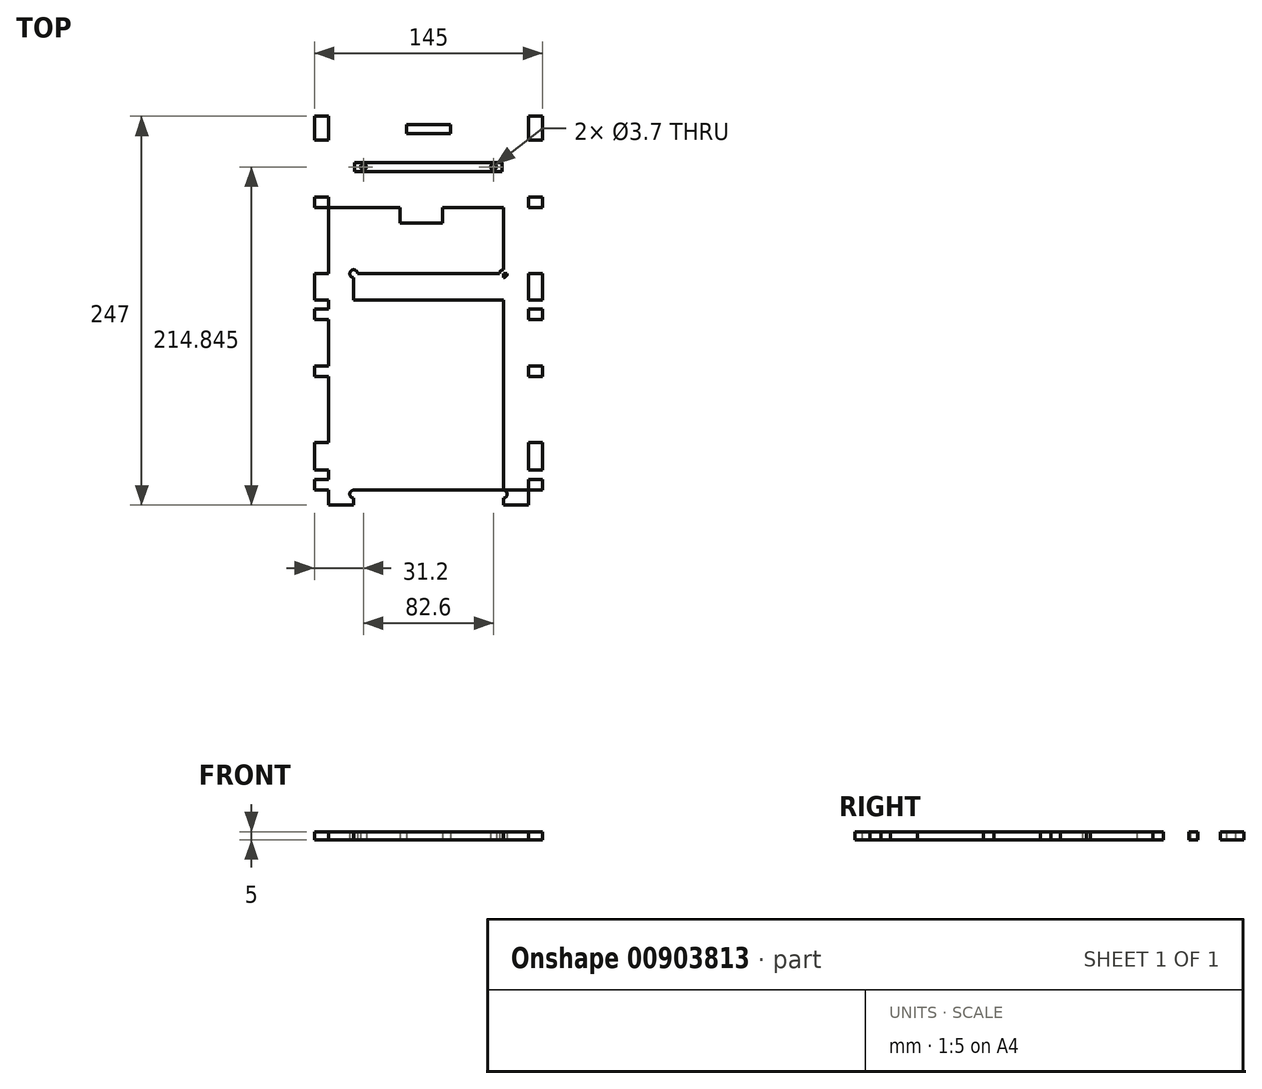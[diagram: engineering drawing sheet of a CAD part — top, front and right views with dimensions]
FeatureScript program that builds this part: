
annotation { "Feature Type Name" : "Feature", "Feature Type Description" : "" }
export const myFeature = defineFeature(function(context is Context, id is Id, definition is map)
    precondition{}
    {
        {
            var Q0;
            Q0=qCreatedBy(makeId("Top.planeOp"),FACE);
            var sketch = newSketch(context, id + "F0", { "sketchPlane" : qUnion([Q0])});
            skLineSegment(sketch, "E0.bottom", {"start": v(-77.4, -23.3) * mm, "end": v(49.6, -23.3) * mm});
            skLineSegment(sketch, "E0.top", {"start": v(-77.4, 223.7) * mm, "end": v(49.6, 223.7) * mm});
            skLineSegment(sketch, "E0.left", {"start": v(-77.4, -23.3) * mm, "end": v(-77.4, 223.7) * mm});
            skLineSegment(sketch, "E0.right", {"start": v(49.6, -23.3) * mm, "end": v(49.6, 223.7) * mm});
            skLineSegment(sketch, "E1", {"start": v(49.6, 223.7) * mm, "end": v(58.6, 223.7) * mm});
            skLineSegment(sketch, "E2", {"start": v(-86.4, 223.7) * mm, "end": v(-77.4, 223.7) * mm});
            skLineSegment(sketch, "E3", {"start": v(58.6, 223.7) * mm, "end": v(58.6, 208.7) * mm});
            skLineSegment(sketch, "E4", {"start": v(58.6, 208.7) * mm, "end": v(49.6, 208.7) * mm});
            skLineSegment(sketch, "E5", {"start": v(49.6, 208.7) * mm, "end": v(49.6, 172.5) * mm});
            skLineSegment(sketch, "E6", {"start": v(58.6, 172.5) * mm, "end": v(49.6, 172.5) * mm});
            skLineSegment(sketch, "E7", {"start": v(58.6, 172.5) * mm, "end": v(58.6, 165.8) * mm});
            skLineSegment(sketch, "E8", {"start": v(58.6, 165.8) * mm, "end": v(49.6, 165.8) * mm});
            skLineSegment(sketch, "E9", {"start": v(49.6, 165.8) * mm, "end": v(49.6, 123.8) * mm});
            skLineSegment(sketch, "E10", {"start": v(49.6, 123.8) * mm, "end": v(58.6, 123.8) * mm});
            skLineSegment(sketch, "E11", {"start": v(58.6, 107.1) * mm, "end": v(58.6, 123.8) * mm});
            skLineSegment(sketch, "E12", {"start": v(58.6, 107.1) * mm, "end": v(49.6, 107.1) * mm});
            skLineSegment(sketch, "E13", {"start": v(49.6, 107.1) * mm, "end": v(49.6, 101.2) * mm});
            skLineSegment(sketch, "E14", {"start": v(49.6, 101.2) * mm, "end": v(58.6, 101.2) * mm});
            skLineSegment(sketch, "E15", {"start": v(58.6, 101.2) * mm, "end": v(58.6, 94.5) * mm});
            skLineSegment(sketch, "E16", {"start": v(58.6, 94.5) * mm, "end": v(49.6, 94.5) * mm});
            skLineSegment(sketch, "E17", {"start": v(49.6, 94.5) * mm, "end": v(49.6, 65.1) * mm});
            skLineSegment(sketch, "E18", {"start": v(49.6, 65.1) * mm, "end": v(58.6, 65.1) * mm});
            skLineSegment(sketch, "E19", {"start": v(58.6, 65.1) * mm, "end": v(58.6, 58.3) * mm});
            skLineSegment(sketch, "E20", {"start": v(49.6, 58.3) * mm, "end": v(58.6, 58.3) * mm});
            skLineSegment(sketch, "E21", {"start": v(49.6, 58.3) * mm, "end": v(49.6, 16.4) * mm});
            skLineSegment(sketch, "E22", {"start": v(49.6, 16.4) * mm, "end": v(58.6, 16.4) * mm});
            skLineSegment(sketch, "E23", {"start": v(58.6, 16.4) * mm, "end": v(58.6, -0.9) * mm});
            skLineSegment(sketch, "E24", {"start": v(58.6, -0.9) * mm, "end": v(49.6, -0.9) * mm});
            skLineSegment(sketch, "E25", {"start": v(49.6, -0.9) * mm, "end": v(49.6, -6.9) * mm});
            skLineSegment(sketch, "E26", {"start": v(49.6, -6.9) * mm, "end": v(58.6, -6.9) * mm});
            skLineSegment(sketch, "E27", {"start": v(49.6, -6.9) * mm, "end": v(49.6, -13.7) * mm});
            skLineSegment(sketch, "E28", {"start": v(49.6, -13.7) * mm, "end": v(58.6, -13.7) * mm});
            skLineSegment(sketch, "E29", {"start": v(58.6, -6.9) * mm, "end": v(58.6, -13.7) * mm});
            skLineSegment(sketch, "E30", {"start": v(49.6, 208.7) * mm, "end": v(-86.4, 208.7) * mm});
            skLineSegment(sketch, "E31", {"start": v(49.6, 172.5) * mm, "end": v(-86.28, 172.5) * mm});
            skLineSegment(sketch, "E32", {"start": v(49.6, 165.8) * mm, "end": v(-86.28, 165.8) * mm});
            skLineSegment(sketch, "E33", {"start": v(49.6, 123.8) * mm, "end": v(-86.4, 123.8) * mm});
            skLineSegment(sketch, "E34", {"start": v(49.6, 107.1) * mm, "end": v(-86.4, 107.1) * mm});
            skLineSegment(sketch, "E35", {"start": v(49.6, 101.2) * mm, "end": v(-86.4, 101.2) * mm});
            skLineSegment(sketch, "E36", {"start": v(49.6, 94.5) * mm, "end": v(-86.4, 94.5) * mm});
            skLineSegment(sketch, "E37", {"start": v(49.6, 65.1) * mm, "end": v(-86.4, 65.1) * mm});
            skLineSegment(sketch, "E38", {"start": v(49.6, 58.3) * mm, "end": v(-86.4, 58.3) * mm});
            skLineSegment(sketch, "E39", {"start": v(49.6, 16.4) * mm, "end": v(-86.4, 16.4) * mm});
            skLineSegment(sketch, "E40", {"start": v(49.6, -0.9) * mm, "end": v(-86.4, -0.9) * mm});
            skLineSegment(sketch, "E41", {"start": v(49.6, -6.9) * mm, "end": v(-86.4, -6.9) * mm});
            skLineSegment(sketch, "E42", {"start": v(49.6, -13.7) * mm, "end": v(-86.4, -13.7) * mm});
            skLineSegment(sketch, "E43", {"start": v(-86.4, -13.7) * mm, "end": v(-86.4, -6.9) * mm});
            skLineSegment(sketch, "E44", {"start": v(-86.4, -0.9) * mm, "end": v(-86.4, 16.4) * mm});
            skLineSegment(sketch, "E45", {"start": v(-86.4, 58.3) * mm, "end": v(-86.4, 65.1) * mm});
            skLineSegment(sketch, "E46", {"start": v(-86.4, 94.5) * mm, "end": v(-86.4, 101.2) * mm});
            skLineSegment(sketch, "E47", {"start": v(-86.4, 107.1) * mm, "end": v(-86.4, 123.8) * mm});
            skLineSegment(sketch, "E48", {"start": v(-86.28, 165.8) * mm, "end": v(-86.28, 172.5) * mm});
            skLineSegment(sketch, "E49", {"start": v(-86.4, 208.7) * mm, "end": v(-86.4, 223.7) * mm});
            skLineSegment(sketch, "E50", {"start": v(49.6, 223.7) * mm, "end": v(49.6, 218.3) * mm});
            skLineSegment(sketch, "E51", {"start": v(49.6, 218.3) * mm, "end": v(-77.4, 218.3) * mm});
            skLineSegment(sketch, "E52", {"start": v(-77.4, 212.6) * mm, "end": v(-77.4, 218.3) * mm});
            skLineSegment(sketch, "E53", {"start": v(-77.4, 212.6) * mm, "end": v(49.6, 212.6) * mm});
            skLineSegment(sketch, "E54", {"start": v(49.6, 212.6) * mm, "end": v(40.9, 212.6) * mm});
            skLineSegment(sketch, "E55", {"start": v(40.9, 212.6) * mm, "end": v(40.9, 218.3) * mm});
            skLineSegment(sketch, "E56", {"start": v(-77.4, 212.6) * mm, "end": v(-68.7, 212.6) * mm});
            skLineSegment(sketch, "E57", {"start": v(-68.7, 218.3) * mm, "end": v(-68.7, 212.6) * mm});
            skLineSegment(sketch, "E58", {"start": v(-68.7, 218.3) * mm, "end": v(-58.5, 218.3) * mm});
            skLineSegment(sketch, "E59", {"start": v(-58.5, 218.3) * mm, "end": v(-58.5, 212.6) * mm});
            skLineSegment(sketch, "E60", {"start": v(40.9, 218.3) * mm, "end": v(30.7, 218.3) * mm});
            skLineSegment(sketch, "E61", {"start": v(30.7, 218.3) * mm, "end": v(30.7, 212.6) * mm});
            skLineSegment(sketch, "E62", {"start": v(30.7, 212.6) * mm, "end": v(10.2, 212.6) * mm});
            skLineSegment(sketch, "E63", {"start": v(10.2, 212.6) * mm, "end": v(10.2, 218.3) * mm});
            skLineSegment(sketch, "E64", {"start": v(10.2, 218.3) * mm, "end": v(30.7, 218.3) * mm});
            skLineSegment(sketch, "E65", {"start": v(-58.5, 212.6) * mm, "end": v(-38, 212.6) * mm});
            skLineSegment(sketch, "E66", {"start": v(-38, 218.3) * mm, "end": v(-58.5, 218.3) * mm});
            skLineSegment(sketch, "E67", {"start": v(-38, 218.3) * mm, "end": v(-38, 212.6) * mm});
            skLineSegment(sketch, "E68", {"start": v(-38, 218.3) * mm, "end": v(-27.8, 218.3) * mm});
            skLineSegment(sketch, "E69", {"start": v(-27.8, 212.6) * mm, "end": v(-27.8, 218.3) * mm});
            skLineSegment(sketch, "E70", {"start": v(10.2, 218.3) * mm, "end": v(0, 218.3) * mm});
            skLineSegment(sketch, "E71", {"start": v(0, 212.6) * mm, "end": v(0, 218.3) * mm});
            skLineSegment(sketch, "E72", {"start": v(0, 212.6) * mm, "end": v(10.2, 212.6) * mm});
            skLineSegment(sketch, "E73", {"start": v(-77.4, 223.7) * mm, "end": v(-77.4, 194.4) * mm});
            skLineSegment(sketch, "E74", {"start": v(-77.4, 194.4) * mm, "end": v(49.6, 194.4) * mm});
            skLineSegment(sketch, "E75", {"start": v(49.6, 194.4) * mm, "end": v(49.6, 188.7) * mm});
            skLineSegment(sketch, "E76", {"start": v(49.6, 188.7) * mm, "end": v(-77.4, 188.7) * mm});
            skLineSegment(sketch, "E77", {"start": v(-77.4, 194.4) * mm, "end": v(-70.9, 194.4) * mm});
            skLineSegment(sketch, "E78", {"start": v(-70.9, 194.4) * mm, "end": v(-70.9, 188.7) * mm});
            skLineSegment(sketch, "E79", {"start": v(49.6, 188.7) * mm, "end": v(43.1, 188.7) * mm});
            skLineSegment(sketch, "E80", {"start": v(43.1, 188.7) * mm, "end": v(43.1, 194.4) * mm});
            skLineSegment(sketch, "E81", {"start": v(43.1, 194.4) * mm, "end": v(32.9, 194.4) * mm});
            skLineSegment(sketch, "E82", {"start": v(32.9, 194.4) * mm, "end": v(43.1, 194.4) * mm});
            skLineSegment(sketch, "E83", {"start": v(32.9, 194.4) * mm, "end": v(32.9, 188.7) * mm});
            skLineSegment(sketch, "E84", {"start": v(32.9, 188.7) * mm, "end": v(43.1, 188.7) * mm});
            skLineSegment(sketch, "E85", {"start": v(-70.9, 194.4) * mm, "end": v(-60.7, 194.4) * mm});
            skLineSegment(sketch, "E86", {"start": v(-60.7, 194.4) * mm, "end": v(-60.7, 188.7) * mm});
            skLineSegment(sketch, "E87", {"start": v(-70.9, 188.7) * mm, "end": v(-60.7, 188.7) * mm});
            skLineSegment(sketch, "E88", {"start": v(-60.7, 191.56) * mm, "end": v(-55.2, 191.56) * mm});
            skCircle(sketch, "E89", {"center": v(-55.2, 191.56) * mm, "radius": 1.85 * mm});
            skLineSegment(sketch, "E90", {"start": v(-57.05, 191.56) * mm, "end": v(-60.7, 191.56) * mm});
            skLineSegment(sketch, "E91", {"start": v(32.9, 191.56) * mm, "end": v(27.4, 191.56) * mm});
            skCircle(sketch, "E92", {"center": v(27.4, 191.56) * mm, "radius": 1.85 * mm});
            skLineSegment(sketch, "E93", {"start": v(-58.5, 215.46) * mm, "end": v(-53.5, 215.46) * mm});
            skCircle(sketch, "E94", {"center": v(-53.5, 215.46) * mm, "radius": 1.85 * mm});
            skLineSegment(sketch, "E95", {"start": v(30.7, 215.46) * mm, "end": v(25.7, 215.46) * mm});
            skCircle(sketch, "E96", {"center": v(25.7, 215.46) * mm, "radius": 1.85 * mm});
            skPoint(sketch, "E97.endSnap0", {"position": v(-13.9, 188.7) * mm});
            skLineSegment(sketch, "E98", {"start": v(-77.4, -23.3) * mm, "end": v(-61.4, -23.3) * mm});
            skLineSegment(sketch, "E99", {"start": v(-61.4, -23.3) * mm, "end": v(-61.4, 165.8) * mm});
            skLineSegment(sketch, "E100", {"start": v(49.6, -23.3) * mm, "end": v(33.6, -23.3) * mm});
            skLineSegment(sketch, "E101", {"start": v(33.6, -23.3) * mm, "end": v(33.6, 165.8) * mm});
            skLineSegment(sketch, "E102", {"start": v(-61.4, -23.3) * mm, "end": v(-61.4, -6.9) * mm});
            skLineSegment(sketch, "E103", {"start": v(-61.4, -23.3) * mm, "end": v(-61.4, -16.3) * mm});
            skCircle(sketch, "E104", {"center": v(-61.4, -16.3) * mm, "radius": 2.5 * mm});
            skLineSegment(sketch, "E105", {"start": v(-61.4, -16.3) * mm, "end": v(-61.4, 123.7) * mm});
            skCircle(sketch, "E106", {"center": v(-61.4, 123.7) * mm, "radius": 2.5 * mm});
            skLineSegment(sketch, "E107", {"start": v(33.6, -23.3) * mm, "end": v(33.6, -16.3) * mm});
            skCircle(sketch, "E108", {"center": v(33.6, -16.3) * mm, "radius": 2.5 * mm});
            skLineSegment(sketch, "E109", {"start": v(33.6, -16.3) * mm, "end": v(33.6, 123.7) * mm});
            skCircle(sketch, "E110", {"center": v(33.6, 123.7) * mm, "radius": 2.5 * mm});
            skLineSegment(sketch, "E111", {"start": v(-13.9, 223.7) * mm, "end": v(-13.9, 207.9) * mm});
            skLineSegment(sketch, "E112", {"start": v(-13.9, 202.9) * mm, "end": v(-13.9, 207.9) * mm});
            skCircle(sketch, "E113", {"center": v(-13.9, 202.9) * mm, "radius": 5 * mm});
            skLineSegment(sketch, "E114", {"start": v(-8.34, 172.5) * mm, "end": v(-28.34, 172.5) * mm});
            skLineSegment(sketch, "E115", {"start": v(-18.34, 165.8) * mm, "end": v(-31.84, 165.8) * mm});
            skLineSegment(sketch, "E116", {"start": v(-31.84, 165.8) * mm, "end": v(-31.84, 155.8) * mm});
            skLineSegment(sketch, "E117", {"start": v(-31.84, 155.8) * mm, "end": v(-4.84, 155.8) * mm});
            skLineSegment(sketch, "E118", {"start": v(-4.84, 155.8) * mm, "end": v(-4.84, 165.8) * mm});
            skSolve(sketch);
        }
        {
            var Q0;
            {var subQ5=sQuery(id+"F0.wireOp",EDGE,"E33");var subQ7=sQuery(id+"F0.wireOp",EDGE,"E0.left");var subQ9=makeQuery(id+"F0.imprint","INTERSECT",VERTEX,{"derivedFrom":[subQ7,subQ5]});Q0=makeQuery(id+"F0.imprint","IMPRINT",FACE,{"disambiguationData":[TD([[makeQuery(id+"F0.imprint","IMPRINT",EDGE,{"disambiguationData":[TD([[subQ9,-1.0]])],"derivedFrom":subQ7}),-1.0]])]});}
            var Q1;
            {var subQ1=sQuery(id+"F0.wireOp",EDGE,"E34");var subQ6=sQuery(id+"F0.wireOp",EDGE,"E0.left");var subQ9=makeQuery(id+"F0.imprint","INTERSECT",VERTEX,{"derivedFrom":[subQ6,subQ1]});Q1=makeQuery(id+"F0.imprint","IMPRINT",FACE,{"disambiguationData":[TD([[makeQuery(id+"F0.imprint","IMPRINT",EDGE,{"disambiguationData":[TD([[subQ9,-1.0]])],"derivedFrom":subQ6}),-1.0]])]});}
            var Q2;
            {var subQ8=sQuery(id+"F0.wireOp",EDGE,"E116");Q2=makeQuery(id+"F0.imprint","IMPRINT",FACE,{"disambiguationData":[TD([[makeQuery(id+"F0.imprint","IMPRINT",EDGE,{"derivedFrom":subQ8}),-1.0]])]});}
            var Q3;
            {var subQ1=sQuery(id+"F0.wireOp",EDGE,"E33");var subQ9=sQuery(id+"F0.wireOp",EDGE,"E110");var subQ10=makeQuery(id+"F0.imprint","INTERSECT",VERTEX,{"disambiguationData":[OD(1.0)],"derivedFrom":[subQ1,subQ9]});Q3=makeQuery(id+"F0.imprint","IMPRINT",FACE,{"disambiguationData":[TD([[makeQuery(id+"F0.imprint","IMPRINT",EDGE,{"disambiguationData":[TD([[subQ10,-1.0]])],"derivedFrom":subQ1}),1.0]])]});}
            var Q4;
            {var subQ0=sQuery(id+"F0.wireOp",EDGE,"E34");var subQ3=sQuery(id+"F0.wireOp",EDGE,"E109");var subQ4=makeQuery(id+"F0.imprint","INTERSECT",VERTEX,{"derivedFrom":[subQ0,subQ3]});Q4=makeQuery(id+"F0.imprint","IMPRINT",FACE,{"disambiguationData":[TD([[makeQuery(id+"F0.imprint","IMPRINT",EDGE,{"disambiguationData":[TD([[subQ4,-1.0]])],"derivedFrom":subQ3}),-1.0]])]});}
            var Q5;
            {var subQ0=sQuery(id+"F0.wireOp",EDGE,"E10");Q5=makeQuery(id+"F0.imprint","IMPRINT",FACE,{"disambiguationData":[TD([[makeQuery(id+"F0.imprint","IMPRINT",EDGE,{"derivedFrom":subQ0}),-1.0]])]});}
            var Q6;
            {var subQ5=sQuery(id+"F0.wireOp",EDGE,"E47");Q6=makeQuery(id+"F0.imprint","IMPRINT",FACE,{"disambiguationData":[TD([[makeQuery(id+"F0.imprint","IMPRINT",EDGE,{"derivedFrom":subQ5}),-1.0]])]});}
            var Q7;
            {var subQ5=sQuery(id+"F0.wireOp",EDGE,"E46");Q7=makeQuery(id+"F0.imprint","IMPRINT",FACE,{"disambiguationData":[TD([[makeQuery(id+"F0.imprint","IMPRINT",EDGE,{"derivedFrom":subQ5}),-1.0]])]});}
            var Q8;
            {var subQ0=sQuery(id+"F0.wireOp",EDGE,"E36");var subQ1=sQuery(id+"F0.wireOp",EDGE,"E0.left");var subQ2=makeQuery(id+"F0.imprint","INTERSECT",VERTEX,{"derivedFrom":[subQ1,subQ0]});Q8=makeQuery(id+"F0.imprint","IMPRINT",FACE,{"disambiguationData":[TD([[makeQuery(id+"F0.imprint","IMPRINT",EDGE,{"disambiguationData":[TD([[subQ2,-1.0]])],"derivedFrom":subQ1}),-1.0]])]});}
            var Q9;
            {var subQ0=sQuery(id+"F0.wireOp",EDGE,"E35");var subQ1=sQuery(id+"F0.wireOp",EDGE,"E0.left");var subQ2=makeQuery(id+"F0.imprint","INTERSECT",VERTEX,{"derivedFrom":[subQ1,subQ0]});Q9=makeQuery(id+"F0.imprint","IMPRINT",FACE,{"disambiguationData":[TD([[makeQuery(id+"F0.imprint","IMPRINT",EDGE,{"disambiguationData":[TD([[subQ2,-1.0]])],"derivedFrom":subQ1}),-1.0]])]});}
            var Q10;
            {var subQ0=sQuery(id+"F0.wireOp",EDGE,"E109");var subQ1=sQuery(id+"F0.wireOp",EDGE,"E34");var subQ2=makeQuery(id+"F0.imprint","INTERSECT",VERTEX,{"derivedFrom":[subQ1,subQ0]});Q10=makeQuery(id+"F0.imprint","IMPRINT",FACE,{"disambiguationData":[TD([[makeQuery(id+"F0.imprint","IMPRINT",EDGE,{"disambiguationData":[TD([[subQ2,-1.0]])],"derivedFrom":subQ1}),1.0]])]});}
            var Q11;
            {var subQ0=sQuery(id+"F0.wireOp",EDGE,"E109");var subQ1=sQuery(id+"F0.wireOp",EDGE,"E35");var subQ2=makeQuery(id+"F0.imprint","INTERSECT",VERTEX,{"derivedFrom":[subQ1,subQ0]});Q11=makeQuery(id+"F0.imprint","IMPRINT",FACE,{"disambiguationData":[TD([[makeQuery(id+"F0.imprint","IMPRINT",EDGE,{"disambiguationData":[TD([[subQ2,-1.0]])],"derivedFrom":subQ1}),1.0]])]});}
            var Q12;
            {var subQ0=sQuery(id+"F0.wireOp",EDGE,"E35");var subQ5=sQuery(id+"F0.wireOp",EDGE,"E109");var subQ6=makeQuery(id+"F0.imprint","INTERSECT",VERTEX,{"derivedFrom":[subQ0,subQ5]});Q12=makeQuery(id+"F0.imprint","IMPRINT",FACE,{"disambiguationData":[TD([[makeQuery(id+"F0.imprint","IMPRINT",EDGE,{"disambiguationData":[TD([[subQ6,1.0]])],"derivedFrom":subQ5}),-1.0]])]});}
            var Q13;
            {var subQ0=sQuery(id+"F0.wireOp",EDGE,"E13");Q13=makeQuery(id+"F0.imprint","IMPRINT",FACE,{"disambiguationData":[TD([[makeQuery(id+"F0.imprint","IMPRINT",EDGE,{"derivedFrom":subQ0}),-1.0]])]});}
            var Q14;
            {var subQ0=sQuery(id+"F0.wireOp",EDGE,"E14");Q14=makeQuery(id+"F0.imprint","IMPRINT",FACE,{"disambiguationData":[TD([[makeQuery(id+"F0.imprint","IMPRINT",EDGE,{"derivedFrom":subQ0}),-1.0]])]});}
            var Q15;
            {var subQ1=sQuery(id+"F0.wireOp",EDGE,"E9");Q15=makeQuery(id+"F0.imprint","IMPRINT",FACE,{"disambiguationData":[TD([[makeQuery(id+"F0.imprint","IMPRINT",EDGE,{"derivedFrom":subQ1}),-1.0]])]});}
            var Q16;
            {var subQ0=sQuery(id+"F0.wireOp",EDGE,"E6");Q16=makeQuery(id+"F0.imprint","IMPRINT",FACE,{"disambiguationData":[TD([[makeQuery(id+"F0.imprint","IMPRINT",EDGE,{"derivedFrom":subQ0}),1.0]])]});}
            var Q17;
            {var subQ4=sQuery(id+"F0.wireOp",EDGE,"E114");Q17=makeQuery(id+"F0.imprint","IMPRINT",FACE,{"disambiguationData":[TD([[makeQuery(id+"F0.imprint","IMPRINT",EDGE,{"derivedFrom":subQ4}),1.0]])]});}
            var Q18;
            {var subQ5=sQuery(id+"F0.wireOp",EDGE,"E48");Q18=makeQuery(id+"F0.imprint","IMPRINT",FACE,{"disambiguationData":[TD([[makeQuery(id+"F0.imprint","IMPRINT",EDGE,{"derivedFrom":subQ5}),-1.0]])]});}
            var Q19;
            {var subQ9=sQuery(id+"F0.wireOp",EDGE,"E79");Q19=makeQuery(id+"F0.imprint","IMPRINT",FACE,{"disambiguationData":[TD([[makeQuery(id+"F0.imprint","IMPRINT",EDGE,{"derivedFrom":subQ9}),1.0]])]});}
            var Q20;
            {var subQ0=sQuery(id+"F0.wireOp",EDGE,"E77");Q20=makeQuery(id+"F0.imprint","IMPRINT",FACE,{"disambiguationData":[TD([[makeQuery(id+"F0.imprint","IMPRINT",EDGE,{"derivedFrom":subQ0}),-1.0]])]});}
            var Q21;
            Q21=makeQuery(id+"F0.imprint","IMPRINT",FACE,{"disambiguationData":[TD([[makeQuery(id+"F0.imprint","IMPRINT",EDGE,{"derivedFrom":sQuery(id+"F0.wireOp",EDGE,"E89")}),-1.0]])]});
            var Q22;
            {var subQ0=sQuery(id+"F0.wireOp",EDGE,"E75");Q22=makeQuery(id+"F0.imprint","IMPRINT",FACE,{"disambiguationData":[TD([[makeQuery(id+"F0.imprint","IMPRINT",EDGE,{"derivedFrom":subQ0}),-1.0]])]});}
            var Q23;
            {var subQ0=sQuery(id+"F0.wireOp",EDGE,"E77");Q23=makeQuery(id+"F0.imprint","IMPRINT",FACE,{"disambiguationData":[TD([[makeQuery(id+"F0.imprint","IMPRINT",EDGE,{"derivedFrom":subQ0}),1.0]])]});}
            var Q24;
            {var subQ1=sQuery(id+"F0.wireOp",EDGE,"E2");Q24=makeQuery(id+"F0.imprint","IMPRINT",FACE,{"disambiguationData":[TD([[makeQuery(id+"F0.imprint","IMPRINT",EDGE,{"derivedFrom":subQ1}),-1.0]])]});}
            var Q25;
            {var subQ4=sQuery(id+"F0.wireOp",EDGE,"E56");Q25=makeQuery(id+"F0.imprint","IMPRINT",FACE,{"disambiguationData":[TD([[makeQuery(id+"F0.imprint","IMPRINT",EDGE,{"derivedFrom":subQ4}),1.0]])]});}
            var Q26;
            {var subQ7=sQuery(id+"F0.wireOp",EDGE,"E56");Q26=makeQuery(id+"F0.imprint","IMPRINT",FACE,{"disambiguationData":[TD([[makeQuery(id+"F0.imprint","IMPRINT",EDGE,{"derivedFrom":subQ7}),-1.0]])]});}
            var Q27;
            {var subQ0=sQuery(id+"F0.wireOp",EDGE,"E58");Q27=makeQuery(id+"F0.imprint","IMPRINT",FACE,{"disambiguationData":[TD([[makeQuery(id+"F0.imprint","IMPRINT",EDGE,{"derivedFrom":subQ0}),1.0]])]});}
            var Q28;
            {var subQ1=sQuery(id+"F0.wireOp",EDGE,"E65");Q28=makeQuery(id+"F0.imprint","IMPRINT",FACE,{"disambiguationData":[TD([[makeQuery(id+"F0.imprint","IMPRINT",EDGE,{"derivedFrom":subQ1}),1.0]])]});}
            var Q29;
            {var subQ0=sQuery(id+"F0.wireOp",EDGE,"E69");Q29=makeQuery(id+"F0.imprint","IMPRINT",FACE,{"disambiguationData":[TD([[makeQuery(id+"F0.imprint","IMPRINT",EDGE,{"derivedFrom":subQ0}),-1.0]])]});}
            var Q30;
            {var subQ0=sQuery(id+"F0.wireOp",EDGE,"E71");Q30=makeQuery(id+"F0.imprint","IMPRINT",FACE,{"disambiguationData":[TD([[makeQuery(id+"F0.imprint","IMPRINT",EDGE,{"derivedFrom":subQ0}),1.0]])]});}
            var Q31;
            {var subQ0=sQuery(id+"F0.wireOp",EDGE,"E54");Q31=makeQuery(id+"F0.imprint","IMPRINT",FACE,{"disambiguationData":[TD([[makeQuery(id+"F0.imprint","IMPRINT",EDGE,{"derivedFrom":subQ0}),1.0]])]});}
            var Q32;
            {var subQ4=sQuery(id+"F0.wireOp",EDGE,"E50");Q32=makeQuery(id+"F0.imprint","IMPRINT",FACE,{"disambiguationData":[TD([[makeQuery(id+"F0.imprint","IMPRINT",EDGE,{"derivedFrom":subQ4}),-1.0]])]});}
            var Q33;
            {var subQ0=sQuery(id+"F0.wireOp",EDGE,"E62");Q33=makeQuery(id+"F0.imprint","IMPRINT",FACE,{"disambiguationData":[TD([[makeQuery(id+"F0.imprint","IMPRINT",EDGE,{"derivedFrom":subQ0}),-1.0]])]});}
            var Q34;
            {var subQ3=sQuery(id+"F0.wireOp",EDGE,"E54");Q34=makeQuery(id+"F0.imprint","IMPRINT",FACE,{"disambiguationData":[TD([[makeQuery(id+"F0.imprint","IMPRINT",EDGE,{"derivedFrom":subQ3}),-1.0]])]});}
            var Q35;
            Q35=makeQuery(id+"F0.imprint","IMPRINT",FACE,{"disambiguationData":[TD([[makeQuery(id+"F0.imprint","IMPRINT",EDGE,{"derivedFrom":sQuery(id+"F0.wireOp",EDGE,"E1")}),-1.0]])]});
            var Q36;
            {var subQ0=sQuery(id+"F0.wireOp",EDGE,"E109");var subQ1=sQuery(id+"F0.wireOp",EDGE,"E36");var subQ2=makeQuery(id+"F0.imprint","INTERSECT",VERTEX,{"derivedFrom":[subQ1,subQ0]});Q36=makeQuery(id+"F0.imprint","IMPRINT",FACE,{"disambiguationData":[TD([[makeQuery(id+"F0.imprint","IMPRINT",EDGE,{"disambiguationData":[TD([[subQ2,-1.0]])],"derivedFrom":subQ1}),1.0]])]});}
            var Q37;
            {var subQ0=sQuery(id+"F0.wireOp",EDGE,"E37");var subQ1=sQuery(id+"F0.wireOp",EDGE,"E0.left");var subQ2=makeQuery(id+"F0.imprint","INTERSECT",VERTEX,{"derivedFrom":[subQ1,subQ0]});Q37=makeQuery(id+"F0.imprint","IMPRINT",FACE,{"disambiguationData":[TD([[makeQuery(id+"F0.imprint","IMPRINT",EDGE,{"disambiguationData":[TD([[subQ2,-1.0]])],"derivedFrom":subQ1}),-1.0]])]});}
            var Q38;
            {var subQ0=sQuery(id+"F0.wireOp",EDGE,"E17");Q38=makeQuery(id+"F0.imprint","IMPRINT",FACE,{"disambiguationData":[TD([[makeQuery(id+"F0.imprint","IMPRINT",EDGE,{"derivedFrom":subQ0}),-1.0]])]});}
            var Q39;
            {var subQ0=sQuery(id+"F0.wireOp",EDGE,"E37");var subQ5=sQuery(id+"F0.wireOp",EDGE,"E109");var subQ6=makeQuery(id+"F0.imprint","INTERSECT",VERTEX,{"derivedFrom":[subQ0,subQ5]});Q39=makeQuery(id+"F0.imprint","IMPRINT",FACE,{"disambiguationData":[TD([[makeQuery(id+"F0.imprint","IMPRINT",EDGE,{"disambiguationData":[TD([[subQ6,1.0]])],"derivedFrom":subQ5}),-1.0]])]});}
            var Q40;
            {var subQ0=sQuery(id+"F0.wireOp",EDGE,"E18");Q40=makeQuery(id+"F0.imprint","IMPRINT",FACE,{"disambiguationData":[TD([[makeQuery(id+"F0.imprint","IMPRINT",EDGE,{"derivedFrom":subQ0}),-1.0]])]});}
            var Q41;
            {var subQ0=sQuery(id+"F0.wireOp",EDGE,"E38");var subQ1=sQuery(id+"F0.wireOp",EDGE,"E0.left");var subQ2=makeQuery(id+"F0.imprint","INTERSECT",VERTEX,{"derivedFrom":[subQ1,subQ0]});Q41=makeQuery(id+"F0.imprint","IMPRINT",FACE,{"disambiguationData":[TD([[makeQuery(id+"F0.imprint","IMPRINT",EDGE,{"disambiguationData":[TD([[subQ2,-1.0]])],"derivedFrom":subQ1}),-1.0]])]});}
            var Q42;
            {var subQ5=sQuery(id+"F0.wireOp",EDGE,"E45");Q42=makeQuery(id+"F0.imprint","IMPRINT",FACE,{"disambiguationData":[TD([[makeQuery(id+"F0.imprint","IMPRINT",EDGE,{"derivedFrom":subQ5}),-1.0]])]});}
            var Q43;
            {var subQ0=sQuery(id+"F0.wireOp",EDGE,"E39");var subQ1=sQuery(id+"F0.wireOp",EDGE,"E0.left");var subQ2=makeQuery(id+"F0.imprint","INTERSECT",VERTEX,{"derivedFrom":[subQ1,subQ0]});Q43=makeQuery(id+"F0.imprint","IMPRINT",FACE,{"disambiguationData":[TD([[makeQuery(id+"F0.imprint","IMPRINT",EDGE,{"disambiguationData":[TD([[subQ2,-1.0]])],"derivedFrom":subQ1}),-1.0]])]});}
            var Q44;
            {var subQ0=sQuery(id+"F0.wireOp",EDGE,"E109");var subQ1=sQuery(id+"F0.wireOp",EDGE,"E38");var subQ2=makeQuery(id+"F0.imprint","INTERSECT",VERTEX,{"derivedFrom":[subQ1,subQ0]});Q44=makeQuery(id+"F0.imprint","IMPRINT",FACE,{"disambiguationData":[TD([[makeQuery(id+"F0.imprint","IMPRINT",EDGE,{"disambiguationData":[TD([[subQ2,-1.0]])],"derivedFrom":subQ1}),1.0]])]});}
            var Q45;
            {var subQ0=sQuery(id+"F0.wireOp",EDGE,"E21");Q45=makeQuery(id+"F0.imprint","IMPRINT",FACE,{"disambiguationData":[TD([[makeQuery(id+"F0.imprint","IMPRINT",EDGE,{"derivedFrom":subQ0}),-1.0]])]});}
            var Q46;
            {var subQ0=sQuery(id+"F0.wireOp",EDGE,"E109");var subQ1=sQuery(id+"F0.wireOp",EDGE,"E37");var subQ2=makeQuery(id+"F0.imprint","INTERSECT",VERTEX,{"derivedFrom":[subQ1,subQ0]});Q46=makeQuery(id+"F0.imprint","IMPRINT",FACE,{"disambiguationData":[TD([[makeQuery(id+"F0.imprint","IMPRINT",EDGE,{"disambiguationData":[TD([[subQ2,-1.0]])],"derivedFrom":subQ1}),1.0]])]});}
            var Q47;
            {var subQ1=sQuery(id+"F0.wireOp",EDGE,"E98");Q47=makeQuery(id+"F0.imprint","IMPRINT",FACE,{"disambiguationData":[TD([[makeQuery(id+"F0.imprint","IMPRINT",EDGE,{"derivedFrom":subQ1}),1.0]])]});}
            var Q48;
            {var subQ0=sQuery(id+"F0.wireOp",EDGE,"E42");var subQ1=sQuery(id+"F0.wireOp",EDGE,"E0.left");var subQ2=makeQuery(id+"F0.imprint","INTERSECT",VERTEX,{"derivedFrom":[subQ1,subQ0]});Q48=makeQuery(id+"F0.imprint","IMPRINT",FACE,{"disambiguationData":[TD([[makeQuery(id+"F0.imprint","IMPRINT",EDGE,{"disambiguationData":[TD([[subQ2,-1.0]])],"derivedFrom":subQ1}),-1.0]])]});}
            var Q49;
            {var subQ5=sQuery(id+"F0.wireOp",EDGE,"E43");Q49=makeQuery(id+"F0.imprint","IMPRINT",FACE,{"disambiguationData":[TD([[makeQuery(id+"F0.imprint","IMPRINT",EDGE,{"derivedFrom":subQ5}),-1.0]])]});}
            var Q50;
            {var subQ0=sQuery(id+"F0.wireOp",EDGE,"E41");var subQ1=sQuery(id+"F0.wireOp",EDGE,"E0.left");var subQ2=makeQuery(id+"F0.imprint","INTERSECT",VERTEX,{"derivedFrom":[subQ1,subQ0]});Q50=makeQuery(id+"F0.imprint","IMPRINT",FACE,{"disambiguationData":[TD([[makeQuery(id+"F0.imprint","IMPRINT",EDGE,{"disambiguationData":[TD([[subQ2,-1.0]])],"derivedFrom":subQ1}),-1.0]])]});}
            var Q51;
            {var subQ0=sQuery(id+"F0.wireOp",EDGE,"E40");var subQ1=sQuery(id+"F0.wireOp",EDGE,"E0.left");var subQ2=makeQuery(id+"F0.imprint","INTERSECT",VERTEX,{"derivedFrom":[subQ1,subQ0]});Q51=makeQuery(id+"F0.imprint","IMPRINT",FACE,{"disambiguationData":[TD([[makeQuery(id+"F0.imprint","IMPRINT",EDGE,{"disambiguationData":[TD([[subQ2,-1.0]])],"derivedFrom":subQ1}),-1.0]])]});}
            var Q52;
            {var subQ5=sQuery(id+"F0.wireOp",EDGE,"E44");Q52=makeQuery(id+"F0.imprint","IMPRINT",FACE,{"disambiguationData":[TD([[makeQuery(id+"F0.imprint","IMPRINT",EDGE,{"derivedFrom":subQ5}),-1.0]])]});}
            var Q53;
            {var subQ0=sQuery(id+"F0.wireOp",EDGE,"E109");var subQ1=sQuery(id+"F0.wireOp",EDGE,"E39");var subQ2=makeQuery(id+"F0.imprint","INTERSECT",VERTEX,{"derivedFrom":[subQ1,subQ0]});Q53=makeQuery(id+"F0.imprint","IMPRINT",FACE,{"disambiguationData":[TD([[makeQuery(id+"F0.imprint","IMPRINT",EDGE,{"disambiguationData":[TD([[subQ2,-1.0]])],"derivedFrom":subQ1}),1.0]])]});}
            var Q54;
            {var subQ0=sQuery(id+"F0.wireOp",EDGE,"E39");var subQ5=sQuery(id+"F0.wireOp",EDGE,"E109");var subQ6=makeQuery(id+"F0.imprint","INTERSECT",VERTEX,{"derivedFrom":[subQ0,subQ5]});Q54=makeQuery(id+"F0.imprint","IMPRINT",FACE,{"disambiguationData":[TD([[makeQuery(id+"F0.imprint","IMPRINT",EDGE,{"disambiguationData":[TD([[subQ6,1.0]])],"derivedFrom":subQ5}),-1.0]])]});}
            var Q55;
            {var subQ0=sQuery(id+"F0.wireOp",EDGE,"E22");Q55=makeQuery(id+"F0.imprint","IMPRINT",FACE,{"disambiguationData":[TD([[makeQuery(id+"F0.imprint","IMPRINT",EDGE,{"derivedFrom":subQ0}),-1.0]])]});}
            var Q56;
            {var subQ0=sQuery(id+"F0.wireOp",EDGE,"E109");var subQ1=sQuery(id+"F0.wireOp",EDGE,"E40");var subQ2=makeQuery(id+"F0.imprint","INTERSECT",VERTEX,{"derivedFrom":[subQ1,subQ0]});Q56=makeQuery(id+"F0.imprint","IMPRINT",FACE,{"disambiguationData":[TD([[makeQuery(id+"F0.imprint","IMPRINT",EDGE,{"disambiguationData":[TD([[subQ2,-1.0]])],"derivedFrom":subQ1}),1.0]])]});}
            var Q57;
            {var subQ0=sQuery(id+"F0.wireOp",EDGE,"E109");var subQ1=sQuery(id+"F0.wireOp",EDGE,"E41");var subQ2=makeQuery(id+"F0.imprint","INTERSECT",VERTEX,{"derivedFrom":[subQ1,subQ0]});Q57=makeQuery(id+"F0.imprint","IMPRINT",FACE,{"disambiguationData":[TD([[makeQuery(id+"F0.imprint","IMPRINT",EDGE,{"disambiguationData":[TD([[subQ2,-1.0]])],"derivedFrom":subQ1}),1.0]])]});}
            var Q58;
            {var subQ1=sQuery(id+"F0.wireOp",EDGE,"E0.bottom");Q58=makeQuery(id+"F0.imprint","IMPRINT",FACE,{"disambiguationData":[TD([[makeQuery(id+"F0.imprint","IMPRINT",EDGE,{"derivedFrom":subQ1}),1.0]])]});}
            var Q59;
            {var subQ0=sQuery(id+"F0.wireOp",EDGE,"E100");Q59=makeQuery(id+"F0.imprint","IMPRINT",FACE,{"disambiguationData":[TD([[makeQuery(id+"F0.imprint","IMPRINT",EDGE,{"derivedFrom":subQ0}),-1.0]])]});}
            var Q60;
            {var subQ0=sQuery(id+"F0.wireOp",EDGE,"E27");Q60=makeQuery(id+"F0.imprint","IMPRINT",FACE,{"disambiguationData":[TD([[makeQuery(id+"F0.imprint","IMPRINT",EDGE,{"derivedFrom":subQ0}),-1.0]])]});}
            var Q61;
            {var subQ0=sQuery(id+"F0.wireOp",EDGE,"E25");Q61=makeQuery(id+"F0.imprint","IMPRINT",FACE,{"disambiguationData":[TD([[makeQuery(id+"F0.imprint","IMPRINT",EDGE,{"derivedFrom":subQ0}),-1.0]])]});}
            var Q62;
            Q62=makeQuery(id+"F0.imprint","IMPRINT",FACE,{"disambiguationData":[TD([[makeQuery(id+"F0.imprint","IMPRINT",EDGE,{"derivedFrom":sQuery(id+"F0.wireOp",EDGE,"E26")}),-1.0]])]});
            extrude(context, id + "F1", {"entities" : qUnion([Q0, Q1, Q2, Q3, Q4, Q5, Q6, Q7, Q8, Q9, Q10, Q11, Q12, Q13, Q14, Q15, Q16, Q17, Q18, Q19, Q20, Q21, Q22, Q23, Q24, Q25, Q26, Q27, Q28, Q29, Q30, Q31, Q32, Q33, Q34, Q35, Q36, Q37, Q38, Q39, Q40, Q41, Q42, Q43, Q44, Q45, Q46, Q47, Q48, Q49, Q50, Q51, Q52, Q53, Q54, Q55, Q56, Q57, Q58, Q59, Q60, Q61, Q62]), "depth" : 5 * mm, "offsetDistance" : 25 * mm});
        }
    });
